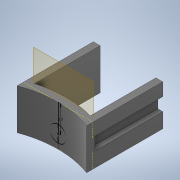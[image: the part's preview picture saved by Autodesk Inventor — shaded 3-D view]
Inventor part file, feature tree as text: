
AUTODESK INVENTOR PART (.ipt)
format: ipt  version: 2020 (Build 240168000, 168)  size: 288,768 bytes
history: native  units: mm
features: sketch x5, projected_geometry x5, extrude x4, other x3
ambient origin geometry x8: Origin, YZ Plane, XZ Plane, XY Plane, X Axis, Y Axis, Z Axis, Center Point
bodies: Body1 (feature_tree)
feature tree (17):
  extrude  "Выдавливание7"  Depth=4.0mm
  other  "РабПлоскость1"
  sketch  "Эскиз6"
  extrude  "Выдавливание8"  Depth=25.5mm
  sketch  "Эскиз7"
  other  "РабПлоскость2"
  sketch  "Эскиз8"
  other  "РабПлоскость3"
  extrude  "Выдавливание11"  Depth=3.0mm
  extrude  "Выдавливание12"  Depth=3.0mm
  sketch  "Эскиз1"
  projected_geometry  "Спроецированная петля4"
  projected_geometry  "Спроецированная петля5"
  projected_geometry  "Спроецированная петля6"
  projected_geometry  "Спроецированная петля7"
  projected_geometry  "Спроецированная петля8"
  sketch  "Эскиз9"
